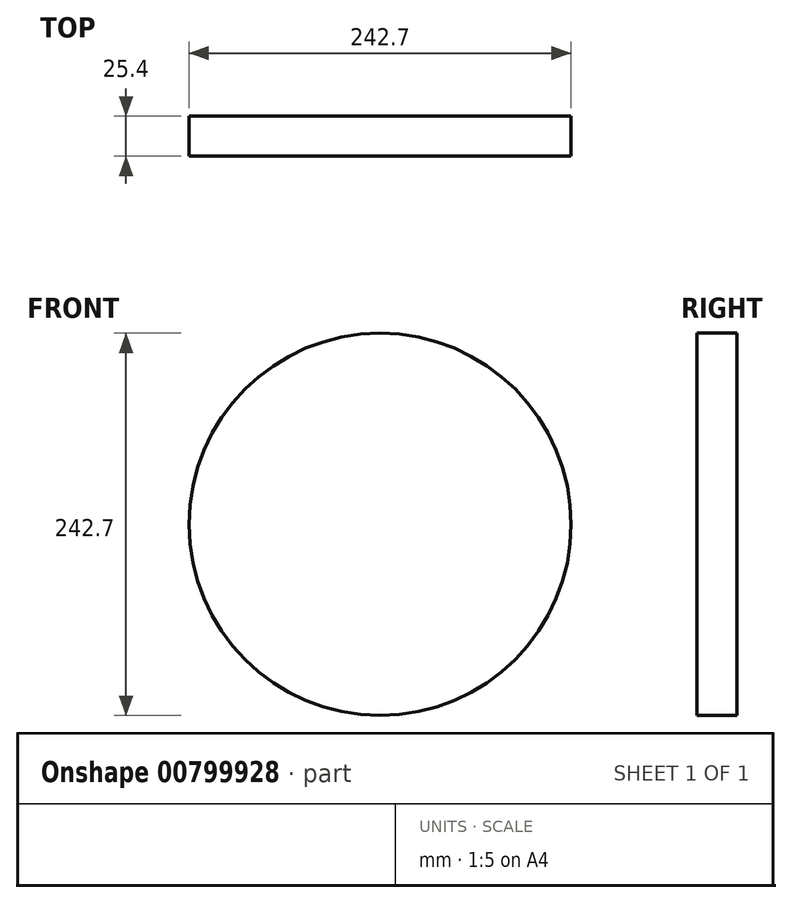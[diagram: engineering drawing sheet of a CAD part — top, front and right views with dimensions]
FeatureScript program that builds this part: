
annotation { "Feature Type Name" : "Feature", "Feature Type Description" : "" }
export const myFeature = defineFeature(function(context is Context, id is Id, definition is map)
    precondition{}
    {
        {
            var Q0;
            Q0=qCreatedBy(makeId("Front.planeOp"),FACE);
            var sketch = newSketch(context, id + "F0", { "sketchPlane" : qUnion([Q0])});
            skCircle(sketch, "E0", {"center": v(0, 0) * mm, "radius": 121.35 * mm});
            skSolve(sketch);
        }
        {
            var Q0;
            Q0=makeQuery(id+"F0.imprint","IMPRINT",FACE,{"disambiguationData":[TD([[makeQuery(id+"F0.imprint","IMPRINT",EDGE,{"derivedFrom":sQuery(id+"F0.wireOp",EDGE,"E0")}),1.0]])]});
            extrude(context, id + "F1", {"entities" : qUnion([Q0]), "depth" : 25.4 * mm, "offsetDistance" : 25.4 * mm});
        }
    });
